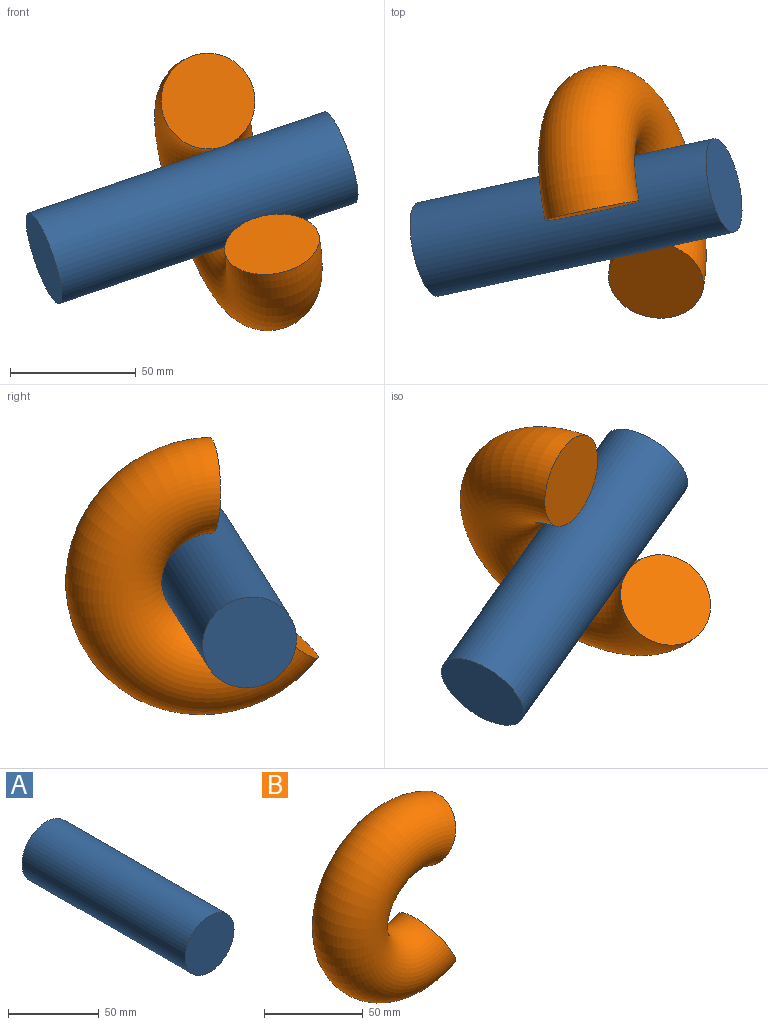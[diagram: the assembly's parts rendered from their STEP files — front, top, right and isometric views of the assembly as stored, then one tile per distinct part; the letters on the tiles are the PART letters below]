
ASSEMBLY  parts=2 mates=1
PART A: 3 faces, bbox 38.1x127x38.1 mm
  f0: cylinder r=19.05mm len=127mm, axis (0,1,0), area 15201.2mm2, adj f1,f2
  f1: plane 38.1x38.1mm, normal (0,-1,0), area 1140.1mm2, adj f0
  f2: plane 38.1x38.1mm, normal (0,1,0), area 1140.1mm2, adj f0
PART B: 3 faces, bbox 89.5x38.1x123.7 mm
  f0: torus R=38.1mm, axis (0,-1,0), area 18545.3mm2, adj f1,f2
  f1: plane 38.1x34.1mm, normal (0.89,0,-0.45), area 1140.1mm2, adj f0
  f2: plane 38.1x34.1mm, normal (0.89,0,0.45), area 1140.1mm2, adj f0
PLACE A rot(axis=(-0.04,-0.41,-0.91),87.9deg) t=(-60.83,32.6,-43.01)mm
PLACE B rot(axis=(-0.04,-0.41,-0.91),87.9deg) t=(-43.85,70.56,-53.88)mm
MATE slider B.f0 <-> A.f0  axis (-0.93,-0.2,-0.32) through (-42.38,36.58,-36.71)mm
